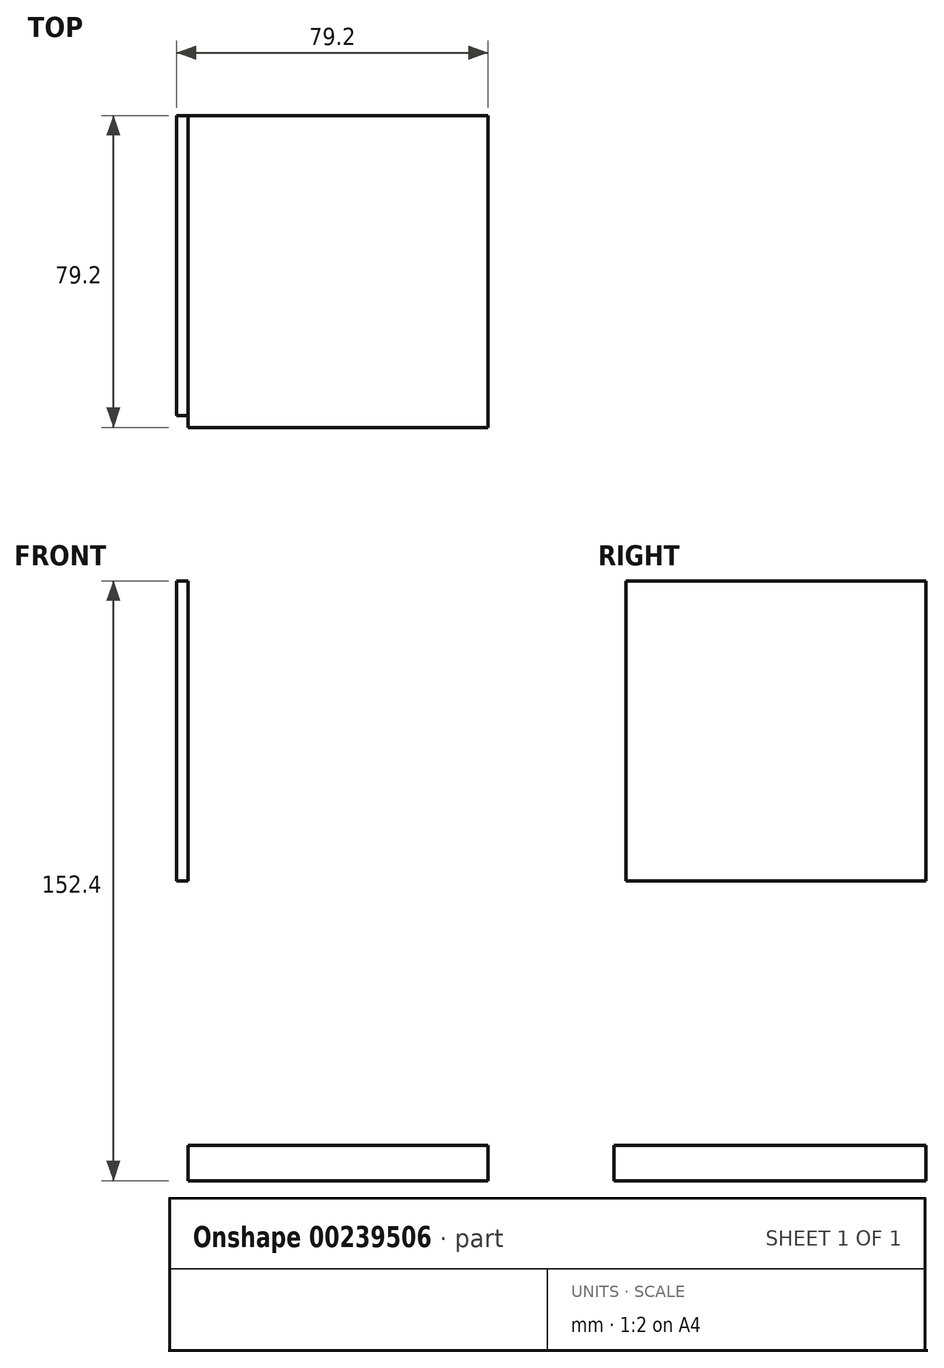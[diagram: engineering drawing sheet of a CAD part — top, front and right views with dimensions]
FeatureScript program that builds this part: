
annotation { "Feature Type Name" : "Feature", "Feature Type Description" : "" }
export const myFeature = defineFeature(function(context is Context, id is Id, definition is map)
    precondition{}
    {
        {
            assignVariable(context, id + "F0", {"name" : "L", "anyValue" : 3});
        }
        {
            var Q0;
            Q0=qCreatedBy(makeId("Top.planeOp"),FACE);
            var sketch = newSketch(context, id + "F1", { "sketchPlane" : qUnion([Q0])});
            skLineSegment(sketch, "E0.bottom", {"start": v(38.1, -38.1) * mm, "end": v(-38.1, -38.1) * mm});
            skLineSegment(sketch, "E0.top", {"start": v(38.1, 38.1) * mm, "end": v(-38.1, 38.1) * mm});
            skLineSegment(sketch, "E0.left", {"start": v(38.1, -38.1) * mm, "end": v(38.1, 38.1) * mm});
            skLineSegment(sketch, "E0.right", {"start": v(-38.1, -38.1) * mm, "end": v(-38.1, 38.1) * mm});
            skPoint(sketch, "E0.middle", {"position": v(0, 0) * mm});
            skSolve(sketch);
        }
        {
            var Q0;
            Q0=makeQuery(id+"F1.imprint","IMPRINT",FACE,{"disambiguationData":[TD([[makeQuery(id+"F1.imprint","IMPRINT",EDGE,{"derivedFrom":sQuery(id+"F1.wireOp",EDGE,"E0.bottom")}),-1.0]])]});
            extrude(context, id + "F2", {"entities" : qUnion([Q0]), "depth" : (getVariable(context, 'L') * (3)) * mm});
        }
        {
            var Q0;
            Q0=makeQuery(id+"F2.opExtrude","SWEPT_FACE",FACE,{"disambiguationData":[OSD([sQuery(id+"F1.wireOp",EDGE,"E0.bottom")])]});
            var sketch = newSketch(context, id + "F3", { "sketchPlane" : qUnion([Q0])});
            skLineSegment(sketch, "E1.bottom", {"start": v(-38.1, 0) * mm, "end": v(38.1, 0) * mm});
            skLineSegment(sketch, "E1.top", {"start": v(-38.1, 76.2) * mm, "end": v(38.1, 76.2) * mm});
            skLineSegment(sketch, "E1.left", {"start": v(-38.1, 0) * mm, "end": v(-38.1, 76.2) * mm});
            skLineSegment(sketch, "E1.right", {"start": v(38.1, 0) * mm, "end": v(38.1, 76.2) * mm});
            skSolve(sketch);
        }
        {
            var Q0;
            Q0=makeQuery(id+"F3.imprint","IMPRINT",FACE,{"disambiguationData":[TD([[makeQuery(id+"F3.imprint","IMPRINT",EDGE,{"derivedFrom":sQuery(id+"F3.wireOp",EDGE,"E1.bottom")}),-1.0]])]});
            extrude(context, id + "F4", {"entities" : qUnion([Q0]), "operationType" : NewBodyOperationType.ADD, "depth" : (getVariable(context, 'L')) * mm});
        }
        {
            var Q0;
            Q0=makeQuery(id+"F4.boolean.opBoolean","MERGE",FACE,{"derivedFrom":[makeQuery(id+"F2.opExtrude","SWEPT_FACE",FACE,{"disambiguationData":[OSD([sQuery(id+"F1.wireOp",EDGE,"E0.right")])]}),makeQuery(id+"F4.opExtrude","SWEPT_FACE",FACE,{"disambiguationData":[OSD([sQuery(id+"F3.wireOp",EDGE,"E1.left")])]})]});
            var sketch = newSketch(context, id + "F5", { "sketchPlane" : qUnion([Q0])});
            skLineSegment(sketch, "E2.bottom", {"start": v(38.1, 76.2) * mm, "end": v(-38.1, 76.2) * mm});
            skLineSegment(sketch, "E2.top", {"start": v(38.1, 152.4) * mm, "end": v(-38.1, 152.4) * mm});
            skLineSegment(sketch, "E2.left", {"start": v(38.1, 76.2) * mm, "end": v(38.1, 152.4) * mm});
            skLineSegment(sketch, "E2.right", {"start": v(-38.1, 76.2) * mm, "end": v(-38.1, 152.4) * mm});
            skSolve(sketch);
        }
        {
            var Q0;
            Q0=makeQuery(id+"F5.imprint","IMPRINT",FACE,{"disambiguationData":[TD([[makeQuery(id+"F5.imprint","IMPRINT",EDGE,{"derivedFrom":sQuery(id+"F5.wireOp",EDGE,"E2.bottom")}),-1.0]])]});
            extrude(context, id + "F6", {"entities" : qUnion([Q0]), "operationType" : NewBodyOperationType.ADD, "depth" : (getVariable(context, 'L')) * mm});
        }
    });
